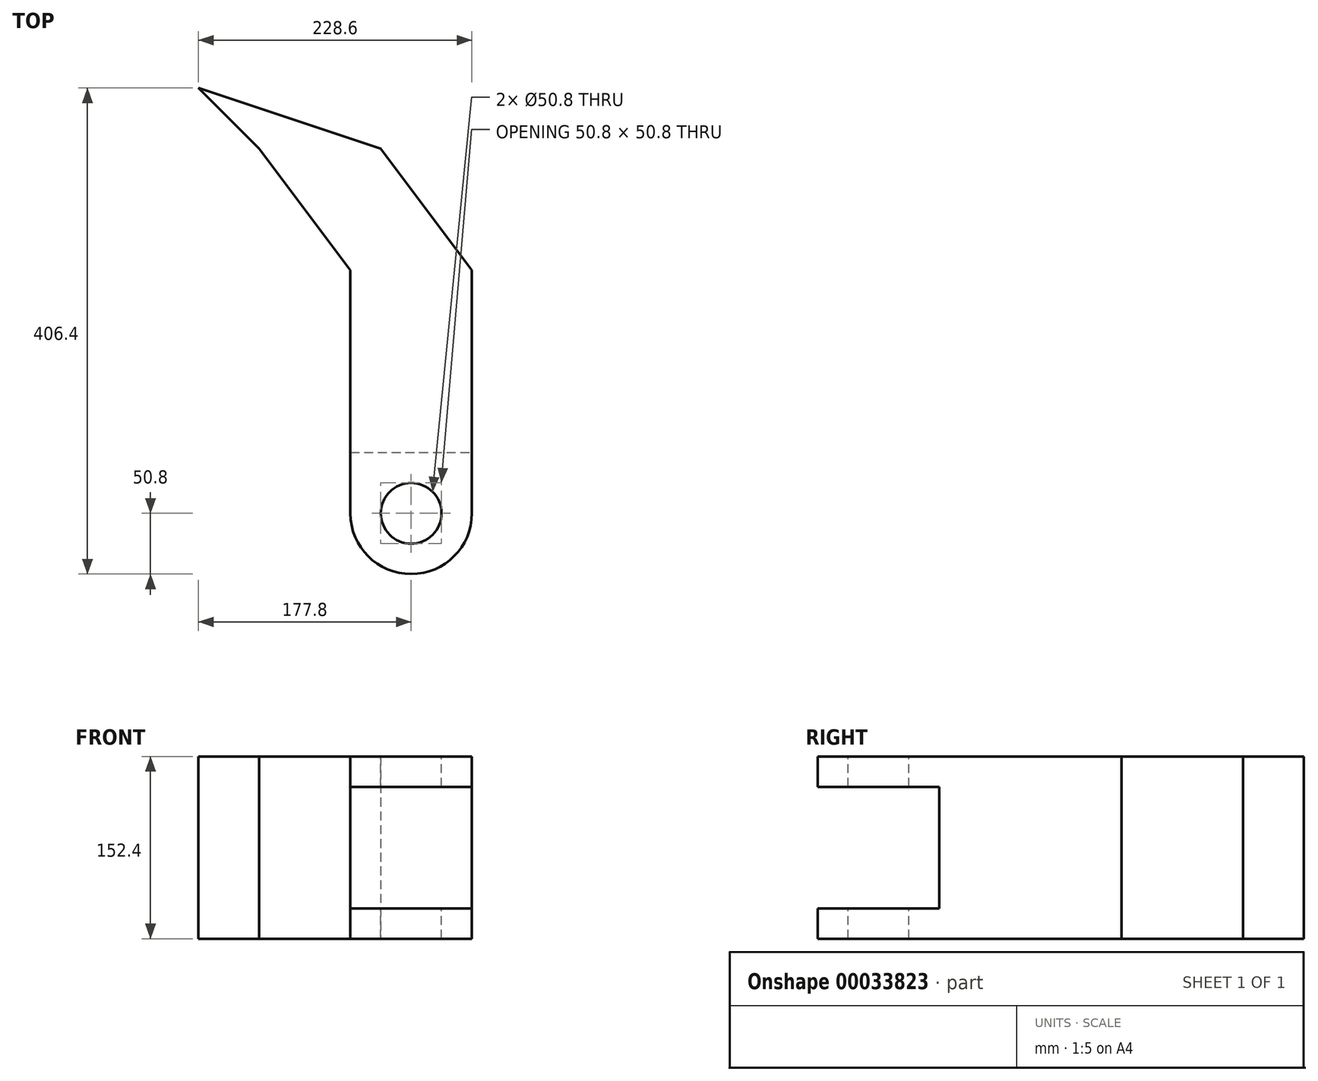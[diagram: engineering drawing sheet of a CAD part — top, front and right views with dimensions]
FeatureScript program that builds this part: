
annotation { "Feature Type Name" : "Feature", "Feature Type Description" : "" }
export const myFeature = defineFeature(function(context is Context, id is Id, definition is map)
    precondition{}
    {
        {
            var Q0;
            Q0=qCreatedBy(makeId("Top.planeOp"),FACE);
            var sketch = newSketch(context, id + "F0", { "sketchPlane" : qUnion([Q0])});
            skLineSegment(sketch, "E0.bottom", {"start": v(0, 0) * mm, "end": v(101.6, 0) * mm});
            skLineSegment(sketch, "E0.top", {"start": v(0, 152.4) * mm, "end": v(101.6, 152.4) * mm});
            skLineSegment(sketch, "E0.left", {"start": v(0, 0) * mm, "end": v(0, 152.4) * mm});
            skLineSegment(sketch, "E0.right", {"start": v(101.6, 0) * mm, "end": v(101.6, 152.4) * mm});
            skLineSegment(sketch, "E1", {"start": v(0, 152.4) * mm, "end": v(-76.2, 254) * mm});
            skLineSegment(sketch, "E2", {"start": v(-76.2, 254) * mm, "end": v(25.4, 254) * mm});
            skLineSegment(sketch, "E3", {"start": v(25.4, 254) * mm, "end": v(101.6, 152.4) * mm});
            skLineSegment(sketch, "E4", {"start": v(-76.2, 254) * mm, "end": v(-127, 304.8) * mm});
            skLineSegment(sketch, "E5", {"start": v(-127, 304.8) * mm, "end": v(25.4, 254) * mm});
            skPoint(sketch, "E6", {"position": v(50.8, 0) * mm});
            skLineSegment(sketch, "E7.top", {"start": v(0, -101.6) * mm, "end": v(101.6, -101.6) * mm});
            skLineSegment(sketch, "E7.left", {"start": v(0, 0) * mm, "end": v(0, -101.6) * mm});
            skLineSegment(sketch, "E7.right", {"start": v(101.6, 0) * mm, "end": v(101.6, -101.6) * mm});
            skSolve(sketch);
        }
        {
            var Q0;
            Q0 = qSketchRegion(id + "F0", true);
            extrude(context, id + "F1", {"entities" : qUnion([Q0]), "depth" : 152.4 * mm});
        }
        {
            var Q0;
            Q0=makeQuery(id+"F1.opExtrude","SWEPT_FACE",FACE,{"disambiguationData":[OSD([sQuery(id+"F0.wireOp",EDGE,"E0.right"),sQuery(id+"F0.wireOp",EDGE,"E7.right")])]});
            var sketch = newSketch(context, id + "F2", { "sketchPlane" : qUnion([Q0])});
            skLineSegment(sketch, "E8.bottom", {"start": v(-101.6, 127) * mm, "end": v(0, 127) * mm});
            skLineSegment(sketch, "E8.top", {"start": v(-101.6, 25.4) * mm, "end": v(0, 25.4) * mm});
            skLineSegment(sketch, "E8.left", {"start": v(-101.6, 127) * mm, "end": v(-101.6, 25.4) * mm});
            skLineSegment(sketch, "E8.right", {"start": v(0, 127) * mm, "end": v(0, 25.4) * mm});
            skSolve(sketch);
        }
        {
            var Q0;
            Q0 = qSketchRegion(id + "F2", true);
            extrude(context, id + "F3", {"entities" : qUnion([Q0]), "operationType" : NewBodyOperationType.REMOVE, "endBound" : BoundingType.THROUGH_ALL, "oppositeDirection" : true, "depth" : 25.4 * mm});
        }
        {
            var Q0;
            Q0=makeQuery(id+"F1.opExtrude","CAP_FACE",FACE,{"disambiguationData":[OSD([sQuery(id+"F0.wireOp",EDGE,"E0.left"),sQuery(id+"F0.wireOp",EDGE,"E0.right"),sQuery(id+"F0.wireOp",EDGE,"E1"),sQuery(id+"F0.wireOp",EDGE,"E3"),sQuery(id+"F0.wireOp",EDGE,"E4"),sQuery(id+"F0.wireOp",EDGE,"E5"),sQuery(id+"F0.wireOp",EDGE,"E7.top"),sQuery(id+"F0.wireOp",EDGE,"E7.left"),sQuery(id+"F0.wireOp",EDGE,"E7.right")])],"isStart":false});
            var sketch = newSketch(context, id + "F4", { "sketchPlane" : qUnion([Q0])});
            skPoint(sketch, "E9", {"position": v(50.8, -101.6) * mm});
            skArc(sketch, "E10", {"start": v(0, -50.8) * mm, "mid": v(50.8, -101.6) * mm, "end": v(101.6, -50.8) * mm});
            skPoint(sketch, "E11", {"position": v(0, -50.8) * mm});
            skPoint(sketch, "E12", {"position": v(101.6, -50.8) * mm});
            skCircle(sketch, "E13", {"center": v(50.8, -50.8) * mm, "radius": 25.4 * mm});
            skSolve(sketch);
        }
        {
            var Q0;
            Q0 = qSketchRegion(id + "F4", true);
            var Q1;
            {var subQ0=makeQuery(id+"F1.opExtrude","CAP_EDGE",EDGE,{"disambiguationData":[OSD([sQuery(id+"F0.wireOp",EDGE,"E7.top")])],"isStart":false});var subQ1=sQuery(id+"F4.wireOp",EDGE,"E10");var subQ2=makeQuery(id+"F4.imprint","INTERSECT",VERTEX,{"derivedFrom":[subQ0,subQ1]});Q1=makeQuery(id+"F4.imprint","IMPRINT",FACE,{"disambiguationData":[TD([[makeQuery(id+"F4.imprint","IMPRINT",EDGE,{"disambiguationData":[TD([[subQ2,1.0]])],"derivedFrom":subQ1}),-1.0]])]});}
            var Q2;
            {var subQ0=makeQuery(id+"F1.opExtrude","CAP_EDGE",EDGE,{"disambiguationData":[OSD([sQuery(id+"F0.wireOp",EDGE,"E7.top")])],"isStart":false});var subQ1=sQuery(id+"F4.wireOp",EDGE,"E10");var subQ2=makeQuery(id+"F4.imprint","INTERSECT",VERTEX,{"derivedFrom":[subQ0,subQ1]});Q2=makeQuery(id+"F4.imprint","IMPRINT",FACE,{"disambiguationData":[TD([[makeQuery(id+"F4.imprint","IMPRINT",EDGE,{"disambiguationData":[TD([[subQ2,-1.0]])],"derivedFrom":subQ1}),-1.0]])]});}
            extrude(context, id + "F5", {"entities" : qUnion([Q0, Q1, Q2]), "operationType" : NewBodyOperationType.REMOVE, "endBound" : BoundingType.THROUGH_ALL, "oppositeDirection" : true, "depth" : 25.4 * mm});
        }
    });
